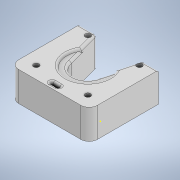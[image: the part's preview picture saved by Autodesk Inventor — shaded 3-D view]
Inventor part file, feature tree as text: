
AUTODESK INVENTOR PART (.ipt)
format: ipt  version: 2021 (Build 250183000, 183)  size: 373,760 bytes
history: native  units: mm
features: sketch x9, extrude x8, fillet x2, other x1, loft x1
ambient origin geometry x8: Origin, YZ Plane, XZ Plane, XY Plane, X Axis, Y Axis, Z Axis, Center Point
bodies: Body1 (feature_tree)
feature tree (21):
  other  "Bryła1"
  extrude  "Wyciągnięcie proste1"  Depth=5.0mm
  extrude  "Wyciągnięcie proste2"  Depth=27.0mm TaperAngle=0.0deg
  extrude  "Wyciągnięcie proste3"  Depth=27.0mm TaperAngle=0.0deg
  extrude  "Wyciągnięcie proste4"  Depth=5.0mm
  extrude  "Wyciągnięcie proste5"  Depth=2.0mm TaperAngle=0.0deg
  extrude  "Wyciągnięcie proste6"  Depth=5.0mm
  sketch  "Szkic19"
  loft  "Wyciągnięcie złożone1"
  sketch  "Szkic34"
  sketch  "Szkic35"
  sketch  "Szkic36"
  sketch  "Szkic44"
  extrude  "Wyciągnięcie proste9"  Depth=5.0mm
  extrude  "Wyciągnięcie proste10"  TaperAngle=0.0deg  [1 undecoded]
  fillet  "Zaokrąglenie3"  Radius=27.0mm
  fillet  "Zaokrąglenie4"  Radius=27.0mm
  sketch  "Szkic14"
  sketch  "Szkic15"
  sketch  "Szkic23"
  sketch  "Szkic45"
note: 1 required parameter value undecoded (feature->parameter linkage not recoverable at this tier; creation-order binding heuristic only, values carry confidence <= 0.55)
